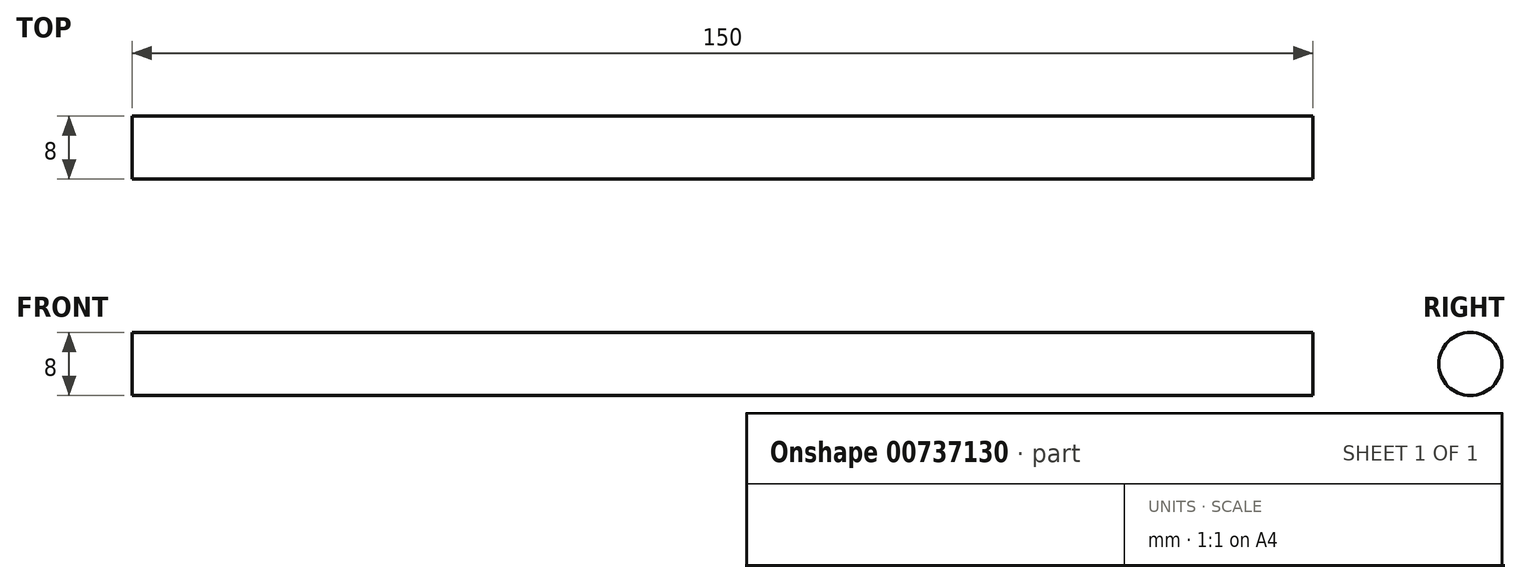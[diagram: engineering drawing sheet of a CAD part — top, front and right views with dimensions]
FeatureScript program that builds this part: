
annotation { "Feature Type Name" : "Feature", "Feature Type Description" : "" }
export const myFeature = defineFeature(function(context is Context, id is Id, definition is map)
    precondition{}
    {
        {
            var Q0;
            Q0=qCreatedBy(makeId("Right.planeOp"),FACE);
            var sketch = newSketch(context, id + "F0", { "sketchPlane" : qUnion([Q0])});
            skCircle(sketch, "E0", {"center": v(0, 0) * mm, "radius": 4 * mm});
            skSolve(sketch);
        }
        {
            var Q0;
            Q0=makeQuery(id+"F0.imprint","IMPRINT",FACE,{"disambiguationData":[TD([[makeQuery(id+"F0.imprint","IMPRINT",EDGE,{"derivedFrom":sQuery(id+"F0.wireOp",EDGE,"E0")}),1.0]])]});
            extrude(context, id + "F1", {"entities" : qUnion([Q0]), "depth" : 75 * mm, "offsetDistance" : 25 * mm, "hasSecondDirection" : true, "secondDirectionOppositeDirection" : true, "secondDirectionDepth" : 75 * mm});
        }
    });
